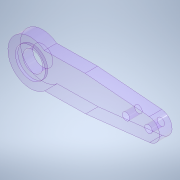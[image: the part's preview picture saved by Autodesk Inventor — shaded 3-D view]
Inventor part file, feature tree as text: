
AUTODESK INVENTOR PART (.ipt)
format: ipt  version: 2020.2 (Build 242310000, 310)  size: 423,424 bytes
history: native  units: mm
features: sketch x9, extrude x8, projected_geometry x5, hole x4, other x2
ambient origin geometry x8: Origin, YZ Plane, XZ Plane, XY Plane, X Axis, Y Axis, Z Axis, Center Point
bodies: Body1 (feature_tree)
feature tree (28):
  other  "ソリッド1"
  sketch  "スケッチ1"
  extrude  "押し出し1"  Depth=5.0mm
  hole  "穴1"  [1 undecoded]
  sketch  "スケッチ2"
  sketch  "スケッチ3"
  sketch  "スケッチ4"
  extrude  "押し出し2"  Depth=6.0mm
  extrude  "押し出し3"  Depth=3.0mm
  hole  "穴2"  [1 undecoded]
  extrude  "押し出し4"  Depth=3.0mm
  sketch  "スケッチ6"
  extrude  "押し出し5"  Depth=3.0mm
  hole  "穴3"  [1 undecoded]
  extrude  "押し出し6"  Depth=3.0mm
  sketch  "スケッチ7"
  sketch  "スケッチ8"
  extrude  "押し出し7"  Depth=19.028919mm
  sketch  "スケッチ9"
  hole  "穴5"  [1 undecoded]
  extrude  "押し出し9"  Depth=9.0mm
  projected_geometry  "投影ループ1"
  projected_geometry  "投影ループ2"
  sketch  "スケッチ5"
  projected_geometry  "投影ループ3"
  projected_geometry  "投影ループ4"
  projected_geometry  "投影ループ5"
  other  "断面エッジを投影1"
note: 4 required parameter values undecoded (feature->parameter linkage not recoverable at this tier; creation-order binding heuristic only, values carry confidence <= 0.55)
